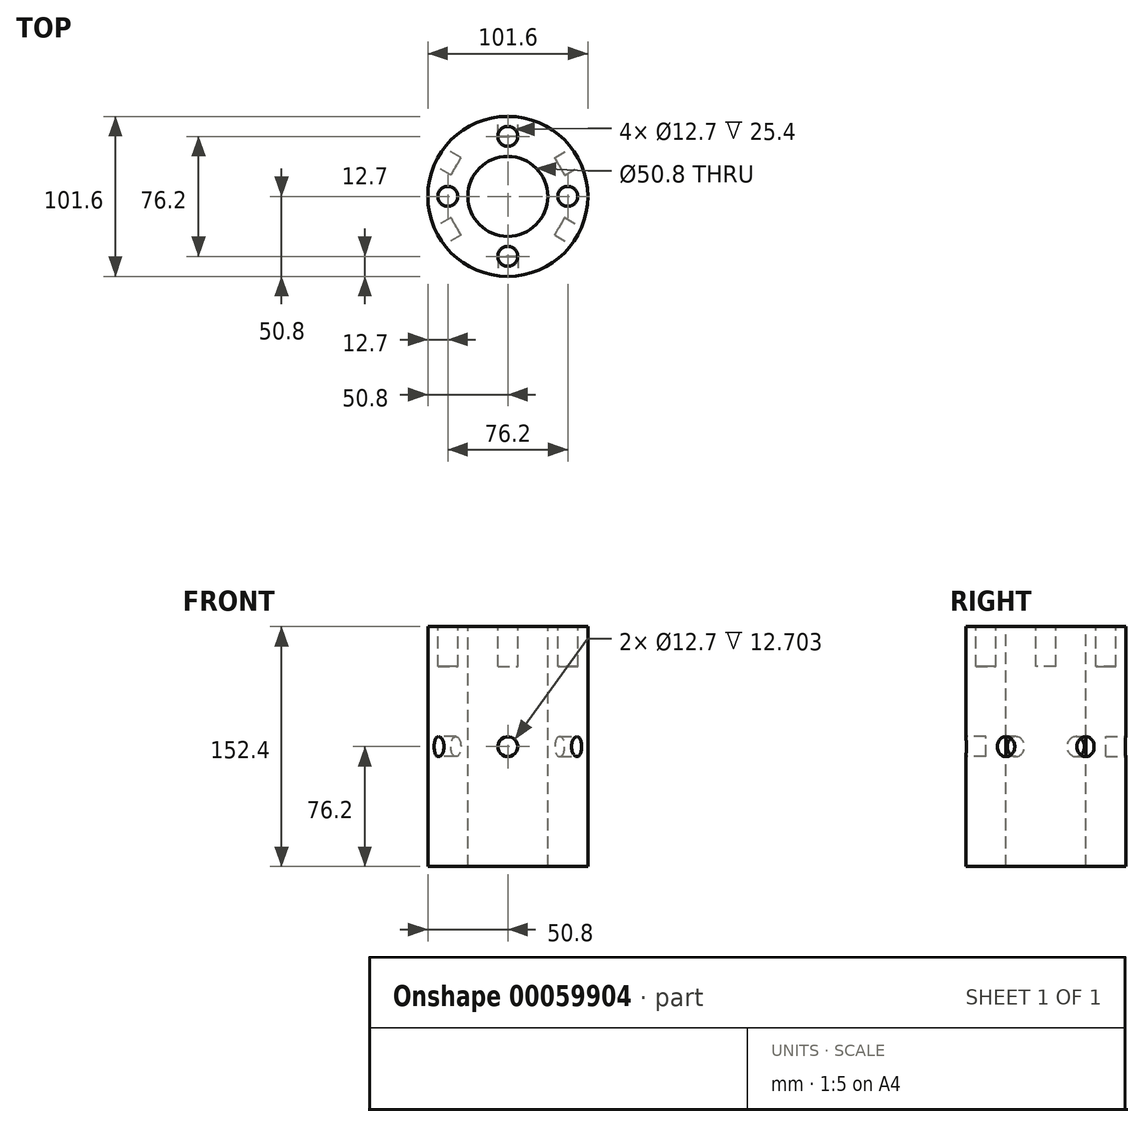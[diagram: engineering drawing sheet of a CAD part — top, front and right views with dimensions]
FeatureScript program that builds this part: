
annotation { "Feature Type Name" : "Feature", "Feature Type Description" : "" }
export const myFeature = defineFeature(function(context is Context, id is Id, definition is map)
    precondition{}
    {
        {
            var Q0;
            Q0=qCreatedBy(makeId("Front.planeOp"),FACE);
            var sketch = newSketch(context, id + "F0", { "sketchPlane" : qUnion([Q0])});
            skLineSegment(sketch, "E0.bottom", {"start": v(0, 76.2) * mm, "end": v(-50.8, 76.2) * mm});
            skLineSegment(sketch, "E0.top", {"start": v(0, -76.2) * mm, "end": v(-50.8, -76.2) * mm});
            skLineSegment(sketch, "E0.left", {"start": v(0, 76.2) * mm, "end": v(0, -76.2) * mm});
            skLineSegment(sketch, "E0.right", {"start": v(-50.8, 76.2) * mm, "end": v(-50.8, -76.2) * mm});
            skSolve(sketch);
        }
        {
            var Q0;
            Q0=makeQuery(id+"F0.imprint","IMPRINT",FACE,{"disambiguationData":[TD([[makeQuery(id+"F0.imprint","IMPRINT",EDGE,{"derivedFrom":sQuery(id+"F0.wireOp",EDGE,"E0.bottom")}),1.0]])]});
            var Q1;
            Q1=sQuery(id+"F0.wireOp",EDGE,"E0.left");
            revolve(context, id + "F1", {"entities" : qUnion([Q0]), "axis" : qUnion([Q1]), "revolveType" : RevolveType.FULL});
        }
        {
            var Q0;
            Q0=qCreatedBy(makeId("Front.planeOp"),FACE);
            var Q1;
            Q1 = qBodyType(qCreatedBy(id + "F3" ,EDGE), BodyType.WIRE);
            cPlane(context, id + "F2", {"entities" : qUnion([Q0, Q1]), "cplaneType" : CPlaneType.OFFSET, "offset" : 50.8 * mm, "width" : 152.4 * mm, "height" : 152.4 * mm});
        }
        {
            var Q0;
            Q0=qCreatedBy(id+"F2.planeOp",FACE);
            var sketch = newSketch(context, id + "F3", { "sketchPlane" : qUnion([Q0])});
            skCircle(sketch, "E1", {"center": v(0, 0) * mm, "radius": 6.35 * mm});
            skSolve(sketch);
        }
        {
            var Q0;
            Q0=makeQuery(id+"F3.imprint","IMPRINT",FACE,{"disambiguationData":[TD([[makeQuery(id+"F3.imprint","IMPRINT",EDGE,{"derivedFrom":sQuery(id+"F3.wireOp",EDGE,"E1")}),1.0]])]});
            extrude(context, id + "F4", {"entities" : qUnion([Q0]), "oppositeDirection" : true, "depth" : 12.7 * mm});
        }
        {
            var Q0;
            Q0=makeQuery(id+"F4.opExtrude","SWEPT_BODY",BODY,{"disambiguationData":[OSD([sQuery(id+"F3.wireOp",EDGE,"E1")])]});
            var Q1;
            Q1=makeQuery(id+"F1.opRevolve","SWEPT_EDGE",EDGE,{"disambiguationData":[OSD([sQuery(id+"F0.wireOp",EDGE,"E0.top"),sQuery(id+"F0.wireOp",EDGE,"E0.right")])]});
            circularPattern(context, id + "F5", {"entities" : qUnion([Q0]), "axis" : qUnion([Q1]), "angle" : 360 * degree, "instanceCount" : 6, "equalSpace" : true});
        }
        {
            var Q0;
            Q0=makeQuery(id+"F4.opExtrude","SWEPT_BODY",BODY,{"disambiguationData":[OSD([sQuery(id+"F3.wireOp",EDGE,"E1")])]});
            var Q1;
            Q1=makeQuery(id+"F5.opPattern","COPY",BODY,{"derivedFrom":makeQuery(id+"F4.opExtrude","SWEPT_BODY",BODY,{"disambiguationData":[OSD([sQuery(id+"F3.wireOp",EDGE,"E1")])]}),"instanceName":"1"});
            var Q2;
            Q2=makeQuery(id+"F5.opPattern","COPY",BODY,{"derivedFrom":makeQuery(id+"F4.opExtrude","SWEPT_BODY",BODY,{"disambiguationData":[OSD([sQuery(id+"F3.wireOp",EDGE,"E1")])]}),"instanceName":"2"});
            var Q3;
            Q3=makeQuery(id+"F5.opPattern","COPY",BODY,{"derivedFrom":makeQuery(id+"F4.opExtrude","SWEPT_BODY",BODY,{"disambiguationData":[OSD([sQuery(id+"F3.wireOp",EDGE,"E1")])]}),"instanceName":"3"});
            var Q4;
            Q4=makeQuery(id+"F5.opPattern","COPY",BODY,{"derivedFrom":makeQuery(id+"F4.opExtrude","SWEPT_BODY",BODY,{"disambiguationData":[OSD([sQuery(id+"F3.wireOp",EDGE,"E1")])]}),"instanceName":"4"});
            var Q5;
            Q5=makeQuery(id+"F5.opPattern","COPY",BODY,{"derivedFrom":makeQuery(id+"F4.opExtrude","SWEPT_BODY",BODY,{"disambiguationData":[OSD([sQuery(id+"F3.wireOp",EDGE,"E1")])]}),"instanceName":"5"});
            var Q6;
            Q6=makeQuery(id+"F1.opRevolve","SWEPT_BODY",BODY,{"disambiguationData":[OSD([sQuery(id+"F0.wireOp",EDGE,"E0.bottom"),sQuery(id+"F0.wireOp",EDGE,"E0.top"),sQuery(id+"F0.wireOp",EDGE,"E0.left"),sQuery(id+"F0.wireOp",EDGE,"E0.right")])]});
            booleanBodies(context, id + "F6", {"operationType" : BooleanOperationType.SUBTRACTION, "tools" : qUnion([Q0, Q1, Q2, Q3, Q4, Q5]), "targets" : qUnion([Q6])});
        }
        {
            var Q0;
            Q0=qCreatedBy(makeId("Top.planeOp"),FACE);
            cPlane(context, id + "F7", {"entities" : qUnion([Q0]), "cplaneType" : CPlaneType.OFFSET, "offset" : 76.2 * mm, "width" : 152.4 * mm, "height" : 152.4 * mm});
        }
        {
            var Q0;
            Q0=qCreatedBy(id+"F7.planeOp",FACE);
            var sketch = newSketch(context, id + "F8", { "sketchPlane" : qUnion([Q0])});
            skCircle(sketch, "E2", {"center": v(0, 0) * mm, "radius": 25.4 * mm});
            skSolve(sketch);
        }
        {
            var Q0;
            Q0=makeQuery(id+"F8.imprint","IMPRINT",FACE,{"disambiguationData":[TD([[makeQuery(id+"F8.imprint","IMPRINT",EDGE,{"derivedFrom":sQuery(id+"F8.wireOp",EDGE,"E2")}),1.0]])]});
            var Q1;
            Q1=sQuery(id+"F8.wireOp",EDGE,"E2");
            extrude(context, id + "F9", {"entities" : qUnion([Q0]), "surfaceEntities" : qUnion([Q1]), "oppositeDirection" : true, "depth" : 152.4 * mm});
        }
        {
            var Q0;
            Q0=makeQuery(id+"F9.opExtrude","SWEPT_BODY",BODY,{"disambiguationData":[OSD([sQuery(id+"F8.wireOp",EDGE,"E2")])]});
            var Q1;
            Q1=makeQuery(id+"F1.opRevolve","SWEPT_BODY",BODY,{"disambiguationData":[OSD([sQuery(id+"F0.wireOp",EDGE,"E0.bottom"),sQuery(id+"F0.wireOp",EDGE,"E0.top"),sQuery(id+"F0.wireOp",EDGE,"E0.left"),sQuery(id+"F0.wireOp",EDGE,"E0.right")])]});
            booleanBodies(context, id + "F10", {"operationType" : BooleanOperationType.SUBTRACTION, "tools" : qUnion([Q0]), "targets" : qUnion([Q1])});
        }
        {
            var Q0;
            Q0=qCreatedBy(id+"F7.planeOp",FACE);
            var sketch = newSketch(context, id + "F11", { "sketchPlane" : qUnion([Q0])});
            skCircle(sketch, "E3", {"center": v(0, 0) * mm, "radius": 38.1 * mm});
            skLineSegment(sketch, "E4", {"start": v(0, 50.8) * mm, "end": v(0, 25.4) * mm});
            skSolve(sketch);
        }
        {
            var Q0;
            Q0=qCreatedBy(id+"F7.planeOp",FACE);
            var sketch = newSketch(context, id + "F12", { "sketchPlane" : qUnion([Q0])});
            skCircle(sketch, "E5", {"center": v(0, 38.1) * mm, "radius": 6.35 * mm});
            skSolve(sketch);
        }
        {
            var Q0;
            Q0=makeQuery(id+"F12.imprint","IMPRINT",FACE,{"disambiguationData":[TD([[makeQuery(id+"F12.imprint","IMPRINT",EDGE,{"derivedFrom":sQuery(id+"F12.wireOp",EDGE,"E5")}),1.0]])]});
            var Q1;
            Q1=sQuery(id+"F12.wireOp",EDGE,"E5");
            extrude(context, id + "F13", {"entities" : qUnion([Q0]), "surfaceEntities" : qUnion([Q1]), "oppositeDirection" : true, "depth" : 25.4 * mm});
        }
        {
            var Q0;
            Q0=makeQuery(id+"F13.opExtrude","SWEPT_BODY",BODY,{"disambiguationData":[OSD([sQuery(id+"F12.wireOp",EDGE,"E5")])]});
            var Q1;
            Q1=sQuery(id+"F0.wireOp",EDGE,"E0.left");
            circularPattern(context, id + "F14", {"entities" : qUnion([Q0]), "axis" : qUnion([Q1]), "angle" : 360 * degree, "instanceCount" : 4, "equalSpace" : true});
        }
        {
            var Q0;
            Q0=makeQuery(id+"F13.opExtrude","SWEPT_BODY",BODY,{"disambiguationData":[OSD([sQuery(id+"F12.wireOp",EDGE,"E5")])]});
            var Q1;
            Q1=makeQuery(id+"F14.opPattern","COPY",BODY,{"derivedFrom":makeQuery(id+"F13.opExtrude","SWEPT_BODY",BODY,{"disambiguationData":[OSD([sQuery(id+"F12.wireOp",EDGE,"E5")])]}),"instanceName":"1"});
            var Q2;
            Q2=makeQuery(id+"F14.opPattern","COPY",BODY,{"derivedFrom":makeQuery(id+"F13.opExtrude","SWEPT_BODY",BODY,{"disambiguationData":[OSD([sQuery(id+"F12.wireOp",EDGE,"E5")])]}),"instanceName":"2"});
            var Q3;
            Q3=makeQuery(id+"F14.opPattern","COPY",BODY,{"derivedFrom":makeQuery(id+"F13.opExtrude","SWEPT_BODY",BODY,{"disambiguationData":[OSD([sQuery(id+"F12.wireOp",EDGE,"E5")])]}),"instanceName":"3"});
            var Q4;
            Q4=makeQuery(id+"F1.opRevolve","SWEPT_BODY",BODY,{"disambiguationData":[OSD([sQuery(id+"F0.wireOp",EDGE,"E0.bottom"),sQuery(id+"F0.wireOp",EDGE,"E0.top"),sQuery(id+"F0.wireOp",EDGE,"E0.left"),sQuery(id+"F0.wireOp",EDGE,"E0.right")])]});
            booleanBodies(context, id + "F15", {"operationType" : BooleanOperationType.SUBTRACTION, "tools" : qUnion([Q0, Q1, Q2, Q3]), "targets" : qUnion([Q4])});
        }
    });
